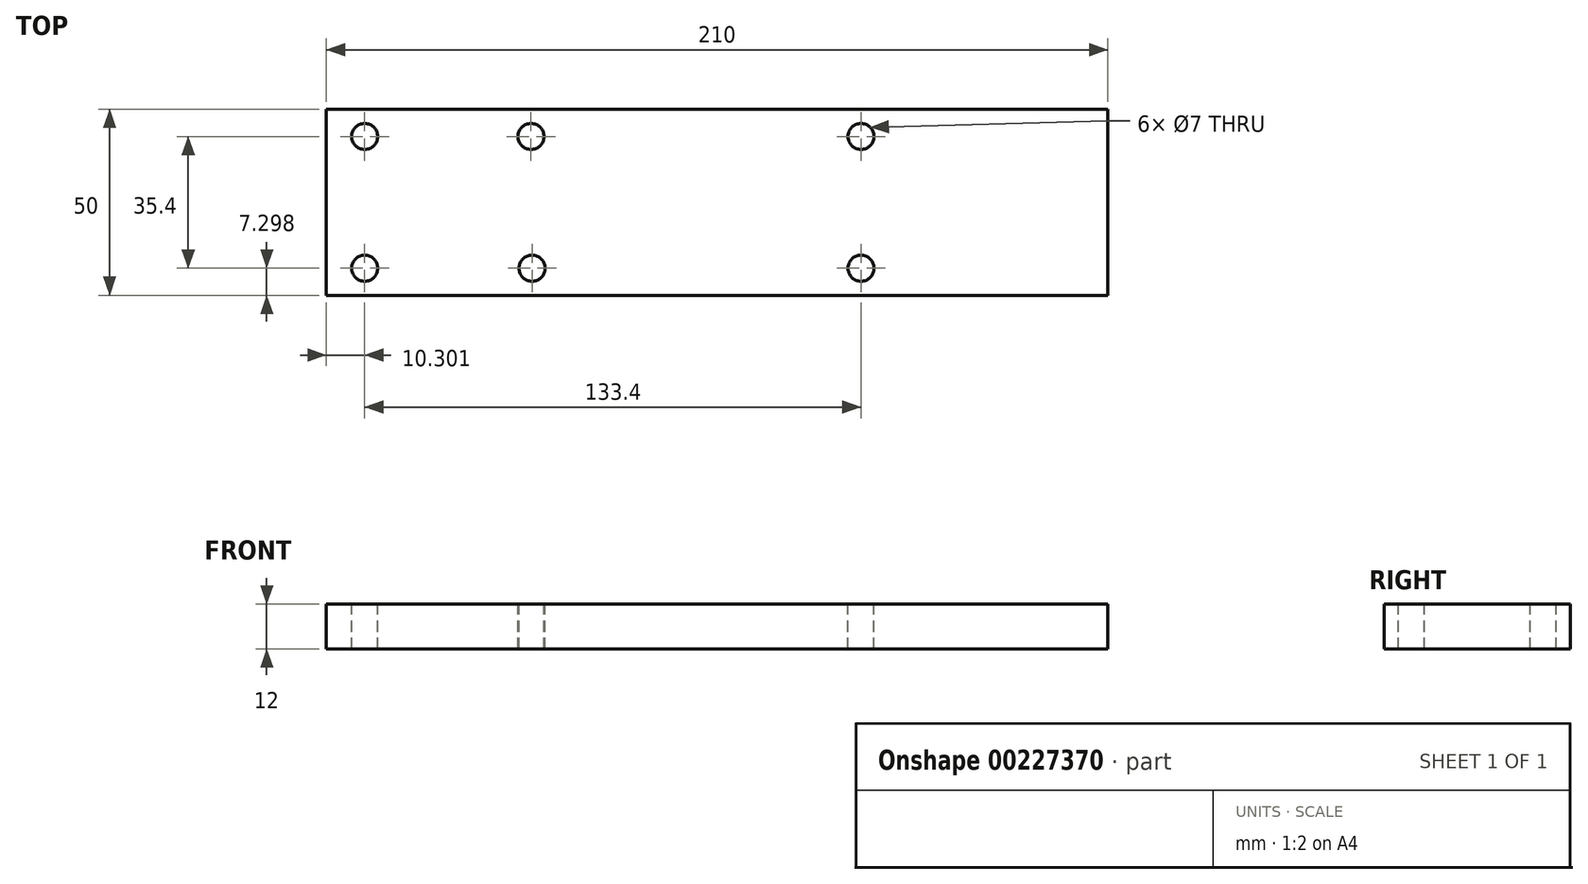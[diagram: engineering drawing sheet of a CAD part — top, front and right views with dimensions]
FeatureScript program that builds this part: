
annotation { "Feature Type Name" : "Feature", "Feature Type Description" : "" }
export const myFeature = defineFeature(function(context is Context, id is Id, definition is map)
    precondition{}
    {
        {
            var Q0;
            Q0=qCreatedBy(makeId("Top.planeOp"),FACE);
            var sketch = newSketch(context, id + "F0", { "sketchPlane" : qUnion([Q0])});
            skLineSegment(sketch, "E0.bottom", {"start": v(-24.3, 20.75) * mm, "end": v(185.7, 20.75) * mm});
            skLineSegment(sketch, "E0.top", {"start": v(-24.3, -29.25) * mm, "end": v(185.7, -29.25) * mm});
            skLineSegment(sketch, "E0.left", {"start": v(-24.3, 20.75) * mm, "end": v(-24.3, -29.25) * mm});
            skLineSegment(sketch, "E0.right", {"start": v(185.7, 20.75) * mm, "end": v(185.7, -29.25) * mm});
            skSolve(sketch);
        }
        {
            var Q0;
            Q0=makeQuery(id+"F0.imprint","IMPRINT",FACE,{"disambiguationData":[TD([[makeQuery(id+"F0.imprint","IMPRINT",EDGE,{"derivedFrom":sQuery(id+"F0.wireOp",EDGE,"E0.bottom")}),-1.0]])]});
            extrude(context, id + "F1", {"entities" : qUnion([Q0]), "offsetDistance" : 25 * mm, "depth" : 12 * mm});
        }
        {
            var Q0;
            Q0=makeQuery(id+"F1.opExtrude","CAP_FACE",FACE,{"disambiguationData":[OSD([sQuery(id+"F0.wireOp",EDGE,"E0.bottom"),sQuery(id+"F0.wireOp",EDGE,"E0.top"),sQuery(id+"F0.wireOp",EDGE,"E0.left"),sQuery(id+"F0.wireOp",EDGE,"E0.right")])],"isStart":false});
            var sketch = newSketch(context, id + "F2", { "sketchPlane" : qUnion([Q0])});
            skCircle(sketch, "E1", {"center": v(-14, 13.45) * mm, "radius": 3.5 * mm});
            skCircle(sketch, "E2", {"center": v(-14, -21.95) * mm, "radius": 3.5 * mm});
            skCircle(sketch, "E3", {"center": v(31, -21.95) * mm, "radius": 3.5 * mm});
            skCircle(sketch, "E4", {"center": v(119.4, 13.45) * mm, "radius": 3.5 * mm});
            skCircle(sketch, "E5", {"center": v(119.4, -21.95) * mm, "radius": 3.5 * mm});
            skSolve(sketch);
        }
        {
            var Q0;
            Q0=makeQuery(id+"F2.imprint","IMPRINT",FACE,{"disambiguationData":[TD([[makeQuery(id+"F2.imprint","IMPRINT",EDGE,{"derivedFrom":sQuery(id+"F2.wireOp",EDGE,"E4")}),1.0]])]});
            var Q1;
            Q1=makeQuery(id+"F2.imprint","IMPRINT",FACE,{"disambiguationData":[TD([[makeQuery(id+"F2.imprint","IMPRINT",EDGE,{"derivedFrom":sQuery(id+"F2.wireOp",EDGE,"E5")}),1.0]])]});
            var Q2;
            Q2=makeQuery(id+"F2.imprint","IMPRINT",FACE,{"disambiguationData":[TD([[makeQuery(id+"F2.imprint","IMPRINT",EDGE,{"derivedFrom":sQuery(id+"F2.wireOp",EDGE,"E3")}),1.0]])]});
            var Q3;
            Q3=makeQuery(id+"F2.imprint","IMPRINT",FACE,{"disambiguationData":[TD([[makeQuery(id+"F2.imprint","IMPRINT",EDGE,{"derivedFrom":sQuery(id+"F2.wireOp",EDGE,"izE0OuF1-xiSJ-FB18-c39p-0N1t3OY4qnCi")}),1.0]])]});
            var Q4;
            Q4=makeQuery(id+"F2.imprint","IMPRINT",FACE,{"disambiguationData":[TD([[makeQuery(id+"F2.imprint","IMPRINT",EDGE,{"derivedFrom":sQuery(id+"F2.wireOp",EDGE,"E1")}),1.0]])]});
            var Q5;
            Q5=makeQuery(id+"F2.imprint","IMPRINT",FACE,{"disambiguationData":[TD([[makeQuery(id+"F2.imprint","IMPRINT",EDGE,{"derivedFrom":sQuery(id+"F2.wireOp",EDGE,"E2")}),1.0]])]});
            var Q6;
            Q6=sQuery(id+"F2.wireOp",EDGE,"E1");
            var Q7;
            Q7=sQuery(id+"F2.wireOp",EDGE,"E2");
            var Q8;
            Q8=sQuery(id+"F2.wireOp",EDGE,"E3");
            var Q9;
            Q9=sQuery(id+"F2.wireOp",EDGE,"izE0OuF1-xiSJ-FB18-c39p-0N1t3OY4qnCi");
            var Q10;
            Q10=sQuery(id+"F2.wireOp",EDGE,"E4");
            var Q11;
            Q11=sQuery(id+"F2.wireOp",EDGE,"E5");
            extrude(context, id + "F3", {"entities" : qUnion([Q0, Q1, Q2, Q3, Q4, Q5]), "operationType" : NewBodyOperationType.REMOVE, "surfaceEntities" : qUnion([Q6, Q7, Q8, Q9, Q10, Q11]), "oppositeDirection" : true, "depth" : 25 * mm});
        }
        {
            var Q0;
            Q0=makeQuery(id+"F1.opExtrude","CAP_FACE",FACE,{"disambiguationData":[OSD([sQuery(id+"F0.wireOp",EDGE,"E0.bottom"),sQuery(id+"F0.wireOp",EDGE,"E0.top"),sQuery(id+"F0.wireOp",EDGE,"E0.left"),sQuery(id+"F0.wireOp",EDGE,"E0.right")])],"isStart":false});
            var sketch = newSketch(context, id + "F4", { "sketchPlane" : qUnion([Q0])});
            skCircle(sketch, "E6", {"center": v(30.7, 13.45) * mm, "radius": 3.5 * mm});
            skSolve(sketch);
        }
        {
            var Q0;
            Q0=qSketchRegion(id+"F4",true);
            extrude(context, id + "F5", {"entities" : qUnion([Q0]), "operationType" : NewBodyOperationType.REMOVE, "oppositeDirection" : true, "depth" : 25 * mm});
        }
    });
